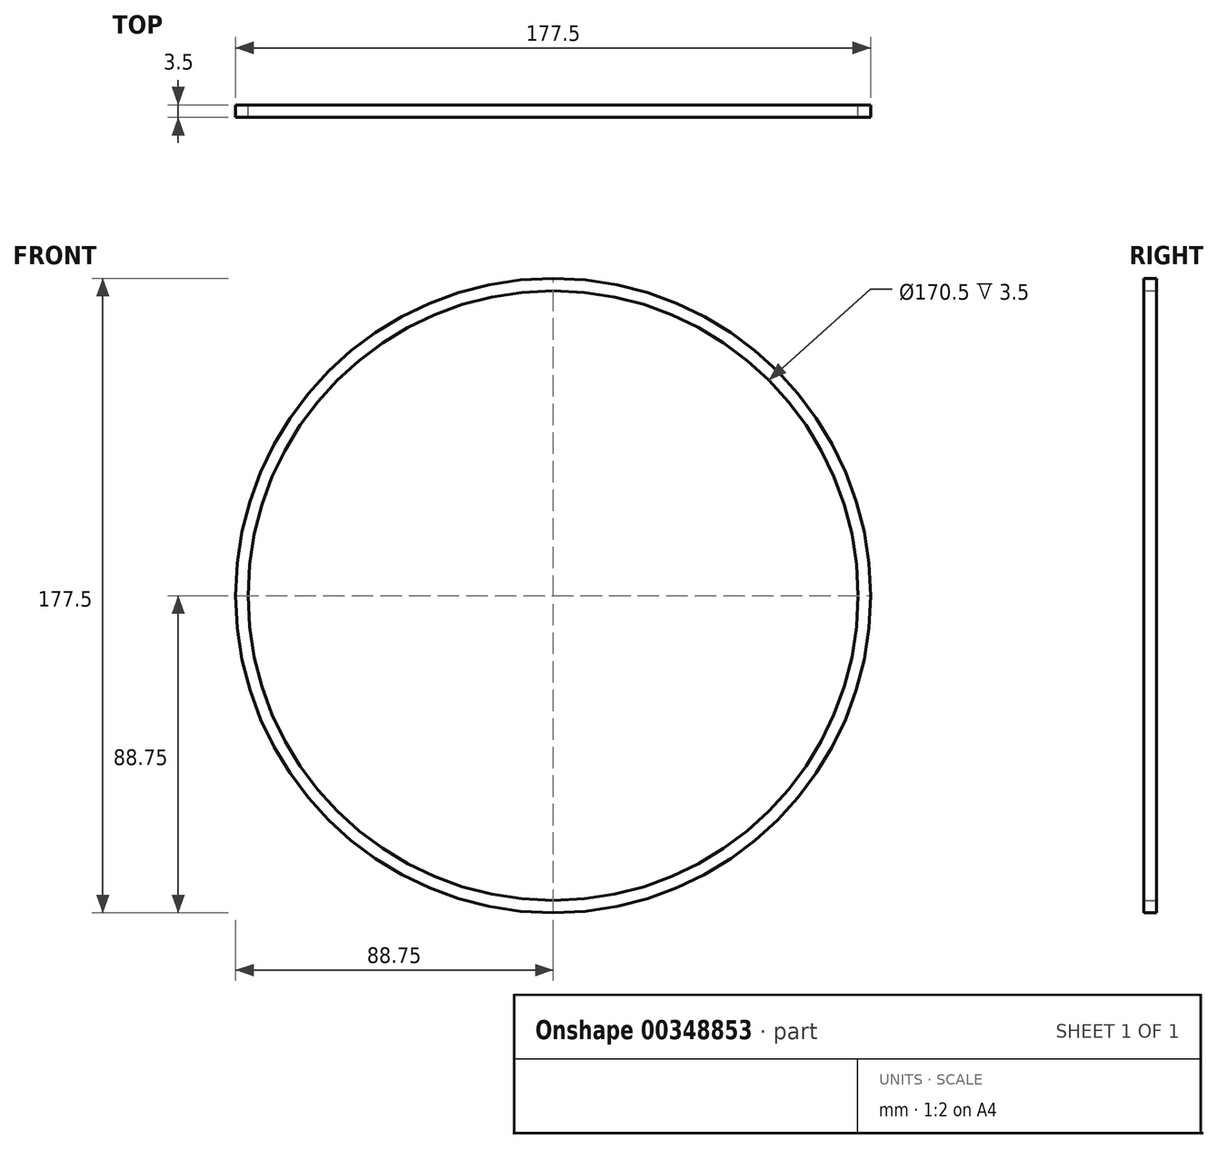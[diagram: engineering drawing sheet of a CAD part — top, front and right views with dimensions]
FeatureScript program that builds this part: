
annotation { "Feature Type Name" : "Feature", "Feature Type Description" : "" }
export const myFeature = defineFeature(function(context is Context, id is Id, definition is map)
    precondition{}
    {
        {
            var Q0;
            Q0=qCreatedBy(makeId("Front.planeOp"),FACE);
            var sketch = newSketch(context, id + "F0", { "sketchPlane" : qUnion([Q0])});
            skCircle(sketch, "E0", {"center": v(0, 0) * mm, "radius": 88.75 * mm});
            skCircle(sketch, "E1", {"center": v(0, 0) * mm, "radius": 85.25 * mm});
            skSolve(sketch);
        }
        {
            var Q0;
            Q0=makeQuery(id+"F0.imprint","IMPRINT",FACE,{"disambiguationData":[TD([[makeQuery(id+"F0.imprint","IMPRINT",EDGE,{"derivedFrom":sQuery(id+"F0.wireOp",EDGE,"E0")}),1.0]])]});
            extrude(context, id + "F1", {"entities" : qUnion([Q0]), "depth" : 3.5 * mm});
        }
    });
